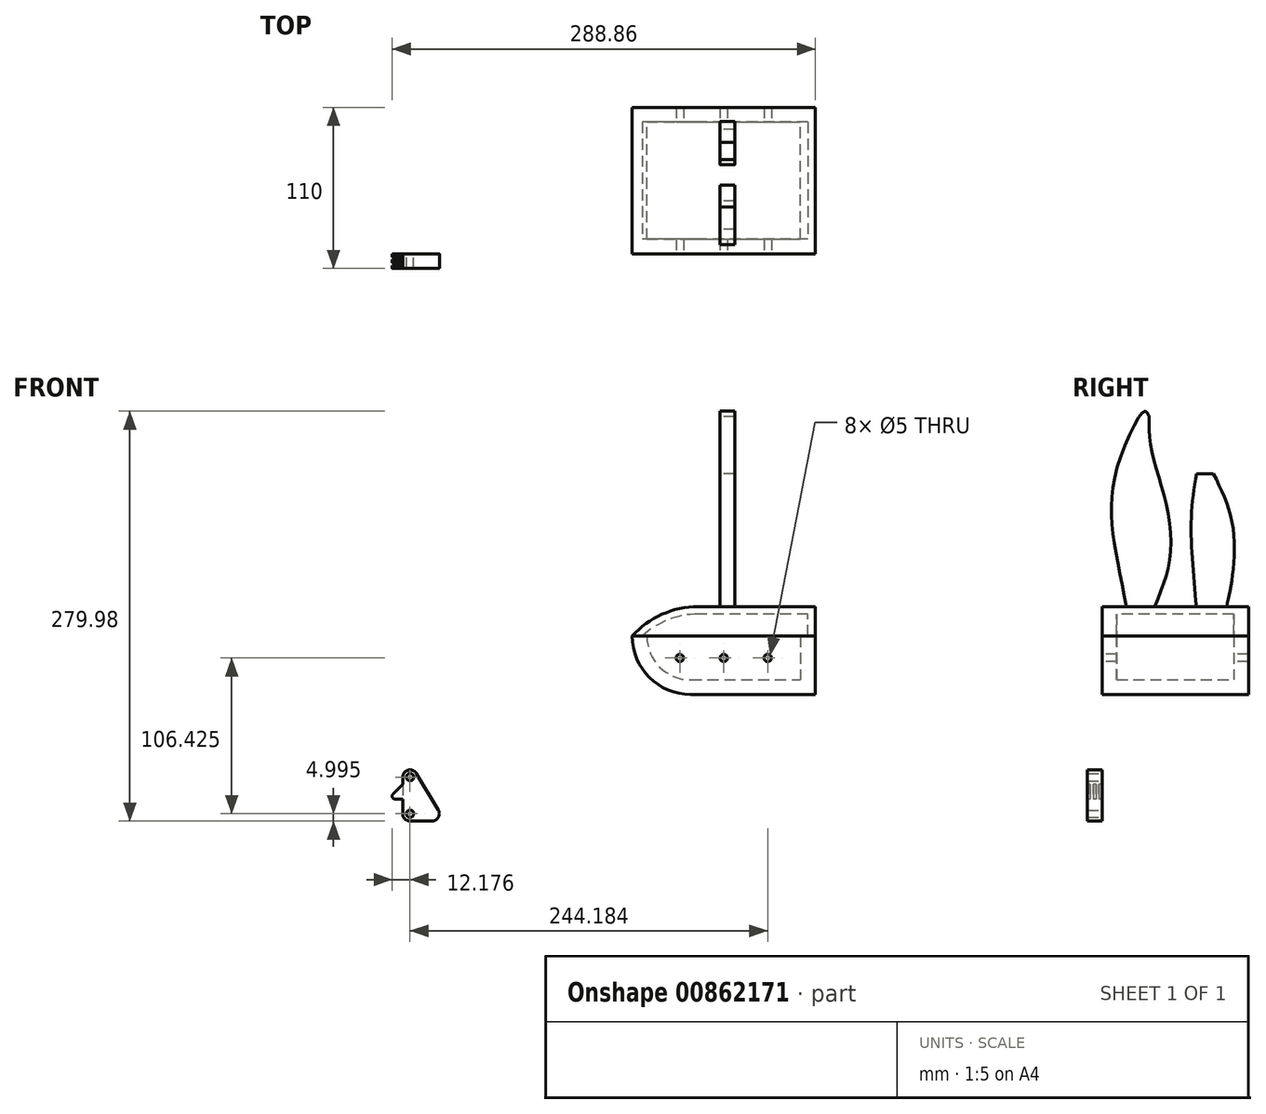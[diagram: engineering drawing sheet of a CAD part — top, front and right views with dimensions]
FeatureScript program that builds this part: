
annotation { "Feature Type Name" : "Feature", "Feature Type Description" : "" }
export const myFeature = defineFeature(function(context is Context, id is Id, definition is map)
    precondition{}
    {
        {
            var Q0;
            Q0=qCreatedBy(makeId("Top.planeOp"),FACE);
            var sketch = newSketch(context, id + "F0", { "sketchPlane" : qUnion([Q0])});
            skLineSegment(sketch, "E0.bottom", {"start": v(0, 0) * mm, "end": v(125, 0) * mm});
            skLineSegment(sketch, "E0.top", {"start": v(0, 100) * mm, "end": v(125, 100) * mm});
            skLineSegment(sketch, "E0.left", {"start": v(0, 0) * mm, "end": v(0, 100) * mm});
            skLineSegment(sketch, "E0.right", {"start": v(125, 0) * mm, "end": v(125, 100) * mm});
            skLineSegment(sketch, "E1.bottom", {"start": v(10, 10) * mm, "end": v(115, 10) * mm});
            skLineSegment(sketch, "E1.top", {"start": v(10, 90) * mm, "end": v(115, 90) * mm});
            skLineSegment(sketch, "E1.left", {"start": v(10, 10) * mm, "end": v(10, 90) * mm});
            skLineSegment(sketch, "E1.right", {"start": v(115, 10) * mm, "end": v(115, 90) * mm});
            skSolve(sketch);
        }
        {
            var Q0;
            Q0=makeQuery(id+"F0.imprint","IMPRINT",FACE,{"disambiguationData":[TD([[makeQuery(id+"F0.imprint","IMPRINT",EDGE,{"derivedFrom":sQuery(id+"F0.wireOp",EDGE,"E0.bottom")}),1.0]])]});
            extrude(context, id + "F1", {"entities" : qUnion([Q0]), "depth" : 30 * mm, "offsetDistance" : 25 * mm});
        }
        {
            var Q0;
            Q0=makeQuery(id+"F1.opExtrude","SWEPT_FACE",FACE,{"disambiguationData":[OSD([sQuery(id+"F0.wireOp",EDGE,"E0.bottom")])]});
            var sketch = newSketch(context, id + "F2", { "sketchPlane" : qUnion([Q0])});
            skCircle(sketch, "E2", {"center": v(62.5, 15) * mm, "radius": 2.5 * mm});
            skCircle(sketch, "E3", {"center": v(92.5, 15) * mm, "radius": 2.5 * mm});
            skCircle(sketch, "E4", {"center": v(32.5, 15) * mm, "radius": 2.5 * mm});
            skSolve(sketch);
        }
        {
            var Q0;
            Q0=makeQuery(id+"F2.imprint","IMPRINT",FACE,{"disambiguationData":[TD([[makeQuery(id+"F2.imprint","IMPRINT",EDGE,{"derivedFrom":sQuery(id+"F2.wireOp",EDGE,"E4")}),1.0]])]});
            var Q1;
            Q1=makeQuery(id+"F2.imprint","IMPRINT",FACE,{"disambiguationData":[TD([[makeQuery(id+"F2.imprint","IMPRINT",EDGE,{"derivedFrom":sQuery(id+"F2.wireOp",EDGE,"E2")}),1.0]])]});
            var Q2;
            Q2=makeQuery(id+"F2.imprint","IMPRINT",FACE,{"disambiguationData":[TD([[makeQuery(id+"F2.imprint","IMPRINT",EDGE,{"derivedFrom":sQuery(id+"F2.wireOp",EDGE,"E3")}),1.0]])]});
            extrude(context, id + "F3", {"entities" : qUnion([Q0, Q1, Q2]), "operationType" : NewBodyOperationType.REMOVE, "endBound" : BoundingType.THROUGH_ALL, "oppositeDirection" : true, "depth" : 25 * mm, "offsetDistance" : 25 * mm});
        }
        {
            var Q0;
            Q0=makeQuery(id+"F1.opExtrude","CAP_FACE",FACE,{"disambiguationData":[OSD([sQuery(id+"F0.wireOp",EDGE,"E0.bottom"),sQuery(id+"F0.wireOp",EDGE,"E0.top"),sQuery(id+"F0.wireOp",EDGE,"E0.left"),sQuery(id+"F0.wireOp",EDGE,"E0.right"),sQuery(id+"F0.wireOp",EDGE,"E1.bottom"),sQuery(id+"F0.wireOp",EDGE,"E1.top"),sQuery(id+"F0.wireOp",EDGE,"E1.left"),sQuery(id+"F0.wireOp",EDGE,"E1.right")])],"isStart":true});
            var sketch = newSketch(context, id + "F4", { "sketchPlane" : qUnion([Q0])});
            skLineSegment(sketch, "E5.bottom", {"start": v(0, 0) * mm, "end": v(125, 0) * mm});
            skLineSegment(sketch, "E5.top", {"start": v(0, -100) * mm, "end": v(125, -100) * mm});
            skLineSegment(sketch, "E5.left", {"start": v(0, 0) * mm, "end": v(0, -100) * mm});
            skLineSegment(sketch, "E5.right", {"start": v(125, 0) * mm, "end": v(125, -100) * mm});
            skSolve(sketch);
        }
        {
            var Q0;
            Q0=makeQuery(id+"F4.imprint","IMPRINT",FACE,{"disambiguationData":[TD([[makeQuery(id+"F4.imprint","IMPRINT",EDGE,{"derivedFrom":sQuery(id+"F4.wireOp",EDGE,"E5.bottom")}),-1.0]])]});
            var Q1;
            Q1=makeQuery(id+"F4.imprint","IMPRINT",FACE,{"disambiguationData":[TD([[makeQuery(id+"F4.imprint","IMPRINT",EDGE,{"derivedFrom":makeQuery(id+"F1.opExtrude","CAP_EDGE",EDGE,{"disambiguationData":[OSD([sQuery(id+"F0.wireOp",EDGE,"E1.bottom")])],"isStart":true})}),-1.0]])]});
            extrude(context, id + "F5", {"entities" : qUnion([Q0, Q1]), "operationType" : NewBodyOperationType.ADD, "depth" : 10 * mm, "offsetDistance" : 25 * mm});
        }
        {
            var Q0;
            Q0=makeQuery(id+"F5.boolean.opBoolean","MERGE",FACE,{"derivedFrom":[makeQuery(id+"F1.opExtrude","SWEPT_FACE",FACE,{"disambiguationData":[OSD([sQuery(id+"F0.wireOp",EDGE,"E0.bottom")])]}),makeQuery(id+"F5.opExtrude","SWEPT_FACE",FACE,{"disambiguationData":[OSD([sQuery(id+"F4.wireOp",EDGE,"E5.bottom")])]})]});
            var sketch = newSketch(context, id + "F6", { "sketchPlane" : qUnion([Q0])});
            skArc(sketch, "E6", {"start": v(0, 30) * mm, "mid": v(11.72, 1.72) * mm, "end": v(40, -10) * mm});
            skLineSegment(sketch, "E7", {"start": v(0, 30) * mm, "end": v(-36.86, 33.31) * mm});
            skLineSegment(sketch, "E8", {"start": v(-36.86, 33.31) * mm, "end": v(-29.77, -57.2) * mm});
            skLineSegment(sketch, "E9", {"start": v(-29.77, -57.2) * mm, "end": v(40, -10) * mm});
            skSolve(sketch);
        }
        {
            var Q0;
            Q0=makeQuery(id+"F6.imprint","IMPRINT",FACE,{"disambiguationData":[TD([[makeQuery(id+"F6.imprint","IMPRINT",EDGE,{"derivedFrom":sQuery(id+"F6.wireOp",EDGE,"E7")}),1.0]])]});
            var Q1;
            {var subQ0=sQuery(id+"F6.wireOp",EDGE,"E6");Q1=makeQuery(id+"F6.imprint","IMPRINT",FACE,{"disambiguationData":[TD([[makeQuery(id+"F6.imprint","IMPRINT",EDGE,{"derivedFrom":subQ0}),-1.0]])]});}
            extrude(context, id + "F7", {"entities" : qUnion([Q0, Q1]), "operationType" : NewBodyOperationType.REMOVE, "oppositeDirection" : true, "depth" : 6666 * mm, "offsetDistance" : 25 * mm});
        }
        {
            var Q0;
            Q0=makeQuery(id+"F1.opExtrude","SWEPT_FACE",FACE,{"disambiguationData":[OSD([sQuery(id+"F0.wireOp",EDGE,"E1.top")])]});
            var sketch = newSketch(context, id + "F8", { "sketchPlane" : qUnion([Q0])});
            skArc(sketch, "E10.0", {"start": v(0, 30) * mm, "mid": v(11.72, 1.72) * mm, "end": v(40, -10) * mm});
            skLineSegment(sketch, "E11", {"start": v(0, 30) * mm, "end": v(10, 30) * mm});
            skLineSegment(sketch, "E12", {"start": v(40, -10) * mm, "end": v(40, 0) * mm});
            skArc(sketch, "E13.0", {"start": v(10, 30) * mm, "mid": v(18.79, 8.79) * mm, "end": v(40, 0) * mm});
            skSolve(sketch);
        }
        {
            var Q0;
            {var subQ5=sQuery(id+"F8.wireOp",EDGE,"E13.0");Q0=makeQuery(id+"F8.imprint","IMPRINT",FACE,{"disambiguationData":[TD([[makeQuery(id+"F8.imprint","IMPRINT",EDGE,{"derivedFrom":subQ5}),-1.0]])]});}
            extrude(context, id + "F9", {"entities" : qUnion([Q0]), "operationType" : NewBodyOperationType.ADD, "depth" : 83.4 * mm, "offsetDistance" : 25 * mm});
        }
        {
            var Q0;
            Q0=makeQuery(id+"F5.boolean.opBoolean","MERGE",FACE,{"derivedFrom":[makeQuery(id+"F1.opExtrude","SWEPT_FACE",FACE,{"disambiguationData":[OSD([sQuery(id+"F0.wireOp",EDGE,"E0.bottom")])]}),makeQuery(id+"F5.opExtrude","SWEPT_FACE",FACE,{"disambiguationData":[OSD([sQuery(id+"F4.wireOp",EDGE,"E5.bottom")])]})]});
            var sketch = newSketch(context, id + "F10", { "sketchPlane" : qUnion([Q0])});
            skLineSegment(sketch, "E14.bottom", {"start": v(125, 30) * mm, "end": v(45, 30) * mm});
            skLineSegment(sketch, "E14.top", {"start": v(125, 50) * mm, "end": v(45, 50) * mm});
            skLineSegment(sketch, "E14.left", {"start": v(125, 30) * mm, "end": v(125, 50) * mm});
            skLineSegment(sketch, "E14.right", {"start": v(45, 30) * mm, "end": v(45, 50) * mm});
            skArc(sketch, "E15", {"start": v(45, 50) * mm, "mid": v(20.38, 44.77) * mm, "end": v(0, 30) * mm});
            skSolve(sketch);
        }
        {
            var Q0;
            {var subQ0=sQuery(id+"F10.wireOp",EDGE,"E14.right");Q0=makeQuery(id+"F10.imprint","IMPRINT",FACE,{"disambiguationData":[TD([[makeQuery(id+"F10.imprint","IMPRINT",EDGE,{"derivedFrom":subQ0}),1.0]])]});}
            var Q1;
            Q1=makeQuery(id+"F10.imprint","IMPRINT",FACE,{"disambiguationData":[TD([[makeQuery(id+"F10.imprint","IMPRINT",EDGE,{"derivedFrom":sQuery(id+"F10.wireOp",EDGE,"E14.bottom")}),1.0]])]});
            extrude(context, id + "F11", {"entities" : qUnion([Q0, Q1]), "oppositeDirection" : true, "depth" : 100 * mm, "offsetDistance" : 25 * mm});
        }
        {
            var Q0;
            Q0=qCreatedBy(makeId("Right.planeOp"),FACE);
            cPlane(context, id + "F12", {"entities" : qUnion([Q0]), "cplaneType" : CPlaneType.OFFSET, "offset" : 60 * mm, "width" : 150 * mm, "height" : 150 * mm});
        }
        {
            var Q0;
            Q0=qCreatedBy(makeId("Front.planeOp"),FACE);
            cPlane(context, id + "F13", {"entities" : qUnion([Q0]), "cplaneType" : CPlaneType.OFFSET, "offset" : 50 * mm, "oppositeDirection" : true, "width" : 150 * mm, "height" : 150 * mm});
        }
        {
            var Q0;
            Q0=qCreatedBy(id+"F12.planeOp",FACE);
            var sketch = newSketch(context, id + "F14", { "sketchPlane" : qUnion([Q0])});
            skFitSpline(sketch, "E16", {"points": [v(85, 49.83) * mm, v(88.38, 66.62) * mm, v(89.24, 105.05) * mm, v(76.14, 140.9) * mm], "startDerivative": vector(13.93, 58.73) * mm, "endDerivative": vector(-44.11, 91.16) * mm});
            skLineSegment(sketch, "E17", {"start": v(76.14, 140.9) * mm, "end": v(64.48, 140.9) * mm});
            skFitSpline(sketch, "E18", {"points": [v(64.48, 140.9) * mm, v(61.06, 113.59) * mm, v(61.63, 82.85) * mm, v(64.48, 49.83) * mm], "startDerivative": vector(-13.6, -84.92) * mm, "endDerivative": vector(9.07, -95.38) * mm});
            skLineSegment(sketch, "E19", {"start": v(85, 49.83) * mm, "end": v(64.48, 49.83) * mm});
            skFitSpline(sketch, "E20", {"points": [v(36.04, 50) * mm, v(45.96, 79.9) * mm, v(43.95, 119.35) * mm, v(33.88, 156.58) * mm, v(32.07, 179.92) * mm], "startDerivative": vector(47.9, 129.75) * mm, "endDerivative": vector(-0.7, 106.5) * mm});
            skFitSpline(sketch, "E21", {"points": [v(16.7, 50) * mm, v(7.12, 103.05) * mm, v(11.14, 147.52) * mm, v(29.26, 183.55) * mm, v(32.07, 179.92) * mm], "startDerivative": vector(-35.74, 181.88) * mm, "endDerivative": vector(23.64, -61.48) * mm});
            skLineSegment(sketch, "E22", {"start": v(36.04, 50) * mm, "end": v(16.7, 50) * mm});
            skSolve(sketch);
        }
        {
            var Q0;
            Q0=makeQuery(id+"F14.imprint","IMPRINT",FACE,{"disambiguationData":[TD([[makeQuery(id+"F14.imprint","IMPRINT",EDGE,{"derivedFrom":sQuery(id+"F14.wireOp",EDGE,"E16")}),1.0]])]});
            var Q1;
            Q1=makeQuery(id+"F14.imprint","IMPRINT",FACE,{"disambiguationData":[TD([[makeQuery(id+"F14.imprint","IMPRINT",EDGE,{"derivedFrom":sQuery(id+"F14.wireOp",EDGE,"E20")}),1.0]])]});
            extrude(context, id + "F15", {"entities" : qUnion([Q0, Q1]), "operationType" : NewBodyOperationType.ADD, "depth" : 10 * mm, "offsetDistance" : 25 * mm});
        }
        {
            var Q0;
            Q0=qCreatedBy(id+"F13.planeOp",FACE);
            var sketch = newSketch(context, id + "F16", { "sketchPlane" : qUnion([Q0])});
            skArc(sketch, "E23.0", {"start": v(45, 50) * mm, "mid": v(20.38, 44.77) * mm, "end": v(0, 30) * mm});
            skLineSegment(sketch, "E24.0", {"start": v(125, 50) * mm, "end": v(45, 50) * mm});
            skArc(sketch, "E25.0", {"start": v(45, 45) * mm, "mid": v(24.57, 41.11) * mm, "end": v(7, 30) * mm});
            skLineSegment(sketch, "E25.1", {"start": v(120, 45) * mm, "end": v(45, 45) * mm});
            skLineSegment(sketch, "E26.0", {"start": v(120, 30) * mm, "end": v(120, 45) * mm});
            skLineSegment(sketch, "E27", {"start": v(120, 30) * mm, "end": v(7, 30) * mm});
            skSolve(sketch);
        }
        {
            var Q0;
            Q0=qSketchRegion(id+"F16",true);
            extrude(context, id + "F17", {"entities" : qUnion([Q0]), "operationType" : NewBodyOperationType.REMOVE, "oppositeDirection" : true, "depth" : 40 * mm, "offsetDistance" : 25 * mm, "hasSecondDirection" : true, "secondDirectionOppositeDirection" : false, "secondDirectionDepth" : 40 * mm});
        }
        {
            var Q0;
            Q0=qCreatedBy(makeId("Front.planeOp"),FACE);
            var sketch = newSketch(context, id + "F18", { "sketchPlane" : qUnion([Q0])});
            skLineSegment(sketch, "E28", {"start": v(-156.68, -66.42) * mm, "end": v(-156.68, -91.42) * mm});
            skArc(sketch, "E29", {"start": v(-156.68, -91.42) * mm, "mid": v(-155.22, -94.96) * mm, "end": v(-151.68, -96.42) * mm});
            skLineSegment(sketch, "E30", {"start": v(-151.68, -96.42) * mm, "end": v(-136.68, -96.42) * mm});
            skArc(sketch, "E31", {"start": v(-136.68, -96.42) * mm, "mid": v(-132.33, -93.89) * mm, "end": v(-132.4, -88.85) * mm});
            skArc(sketch, "E32", {"start": v(-147.4, -63.85) * mm, "mid": v(-153.02, -61.6) * mm, "end": v(-156.68, -66.42) * mm});
            skLineSegment(sketch, "E33", {"start": v(-132.4, -88.85) * mm, "end": v(-147.4, -63.85) * mm});
            skCircle(sketch, "E34", {"center": v(-151.68, -66.42) * mm, "radius": 2.5 * mm});
            skCircle(sketch, "E35", {"center": v(-151.68, -91.42) * mm, "radius": 2.5 * mm});
            skSolve(sketch);
        }
        {
            var Q0;
            Q0=makeQuery(id+"F18.imprint","IMPRINT",FACE,{"disambiguationData":[TD([[makeQuery(id+"F18.imprint","IMPRINT",EDGE,{"derivedFrom":sQuery(id+"F18.wireOp",EDGE,"E28")}),1.0]])]});
            extrude(context, id + "F19", {"entities" : qUnion([Q0]), "depth" : 10 * mm, "offsetDistance" : 25 * mm});
        }
        {
            var Q0;
            Q0=makeQuery(id+"F19.opExtrude","CAP_FACE",FACE,{"disambiguationData":[OSD([sQuery(id+"F18.wireOp",EDGE,"E28"),sQuery(id+"F18.wireOp",EDGE,"E29"),sQuery(id+"F18.wireOp",EDGE,"E30"),sQuery(id+"F18.wireOp",EDGE,"E31"),sQuery(id+"F18.wireOp",EDGE,"E32"),sQuery(id+"F18.wireOp",EDGE,"E33"),sQuery(id+"F18.wireOp",EDGE,"E34"),sQuery(id+"F18.wireOp",EDGE,"E35")])],"isStart":false});
            var sketch = newSketch(context, id + "F20", { "sketchPlane" : qUnion([Q0])});
            skLineSegment(sketch, "E36", {"start": v(-156.68, -71.42) * mm, "end": v(-163.27, -78.01) * mm});
            skLineSegment(sketch, "E37", {"start": v(-161.86, -81.42) * mm, "end": v(-156.68, -81.42) * mm});
            skPoint(sketch, "E38.visualSharp", {"position": v(-166.68, -81.42) * mm});
            skArc(sketch, "E38.filletArc", {"start": v(-163.27, -78.01) * mm, "mid": v(-163.7, -80.2) * mm, "end": v(-161.86, -81.42) * mm});
            skSolve(sketch);
        }
        {
            var Q0;
            {var subQ0=sQuery(id+"F20.wireOp",EDGE,"E36");Q0=makeQuery(id+"F20.imprint","IMPRINT",FACE,{"disambiguationData":[TD([[makeQuery(id+"F20.imprint","IMPRINT",EDGE,{"derivedFrom":subQ0}),1.0]])]});}
            extrude(context, id + "F21", {"entities" : qUnion([Q0]), "operationType" : NewBodyOperationType.ADD, "oppositeDirection" : true, "depth" : 10 * mm, "offsetDistance" : 25 * mm});
        }
        {
            var Q0;
            Q0=makeQuery(id+"F21.opExtrude","SWEPT_FACE",FACE,{"disambiguationData":[OSD([sQuery(id+"F20.wireOp",EDGE,"E37")])]});
            var sketch = newSketch(context, id + "F22", { "sketchPlane" : qUnion([Q0])});
            skLineSegment(sketch, "E39.bottom", {"start": v(-156.68, 2) * mm, "end": v(-173.13, 2) * mm});
            skLineSegment(sketch, "E39.top", {"start": v(-156.68, 4) * mm, "end": v(-173.13, 4) * mm});
            skLineSegment(sketch, "E39.left", {"start": v(-156.68, 2) * mm, "end": v(-156.68, 4) * mm});
            skLineSegment(sketch, "E39.right", {"start": v(-173.13, 2) * mm, "end": v(-173.13, 4) * mm});
            skLineSegment(sketch, "E40.bottom", {"start": v(-156.68, 6) * mm, "end": v(-173.76, 6) * mm});
            skLineSegment(sketch, "E40.top", {"start": v(-156.68, 8) * mm, "end": v(-173.76, 8) * mm});
            skLineSegment(sketch, "E40.left", {"start": v(-156.68, 6) * mm, "end": v(-156.68, 8) * mm});
            skLineSegment(sketch, "E40.right", {"start": v(-173.76, 6) * mm, "end": v(-173.76, 8) * mm});
            skSolve(sketch);
        }
        {
            var Q0;
            {var subQ0=sQuery(id+"F22.wireOp",EDGE,"E40.right");Q0=makeQuery(id+"F22.imprint","IMPRINT",FACE,{"disambiguationData":[TD([[makeQuery(id+"F22.imprint","IMPRINT",EDGE,{"derivedFrom":subQ0}),-1.0]])]});}
            var Q1;
            {var subQ0=sQuery(id+"F22.wireOp",EDGE,"E39.left");Q1=makeQuery(id+"F22.imprint","IMPRINT",FACE,{"disambiguationData":[TD([[makeQuery(id+"F22.imprint","IMPRINT",EDGE,{"derivedFrom":subQ0}),1.0]])]});}
            var Q2;
            {var subQ0=sQuery(id+"F22.wireOp",EDGE,"E40.left");Q2=makeQuery(id+"F22.imprint","IMPRINT",FACE,{"disambiguationData":[TD([[makeQuery(id+"F22.imprint","IMPRINT",EDGE,{"derivedFrom":subQ0}),1.0]])]});}
            var Q3;
            {var subQ0=sQuery(id+"F22.wireOp",EDGE,"E39.right");Q3=makeQuery(id+"F22.imprint","IMPRINT",FACE,{"disambiguationData":[TD([[makeQuery(id+"F22.imprint","IMPRINT",EDGE,{"derivedFrom":subQ0}),-1.0]])]});}
            extrude(context, id + "F23", {"entities" : qUnion([Q0, Q1, Q2, Q3]), "operationType" : NewBodyOperationType.REMOVE, "oppositeDirection" : true, "depth" : 25 * mm, "offsetDistance" : 25 * mm});
        }
    });
